# Revit family: QF_BOURGEAT_Self_Bain_marie_eau_3GN
name_source: partatom
category: Equipement spécialisé
revit_build: Autodesk Revit 2015 (Build: 20140606_1530(x64)
units: mm (PartAtom-declared; Revit-internal decimal feet)

## types (18) — shared parameters
Certification = NF alimentaire
Charge max = 200.00 kg
Cuve à air = Non
Cuve à eau = Oui
Diamètre de Raccordement Eau Adoucie = 21 mm
Diamètre de Raccordement Evacuation = 33 mm
Fabricant = BOURGEAT
Fréquence = 50 Hz
Indice de protection = 21
Longueur hors tout = 1209 mm  [stored 3.96654 ft]
Nature isolant = Laine de verre
Phase = 2
Profondeur hors tout = 820 mm  [stored 2.69029 ft]
Spécification du Fabricant = Bain-marie Oasis
Tension = 230 V
URL catalogue = http://www.bourgeat.fr
lg_etagere = 737 mm  [stored 2.41798 ft]
lg_porte = 379 mm
lg_presentoir = 1097 mm
lgconsole = 1165 mm  [stored 3.82218 ft]
lgmeuble = 1141 mm
zero-valued in all types: Hauteur de Raccordement Eau Adoucie du Sol Finis, Hauteur de Raccordement Evacuation Directe du Sol Finis

## per-type parameters (varying)
| type | Etageres | Hauteur hors tout | Intensité nominale | Modèle | Pieds | Poids net à vide | Presentoir | Puissance électrique  | Reserves | Roues |
| 3GN_baie_libre | Non | 900 mm | 9 A | 851033 | Oui | 150.00 kg | Non | 2100 W | Non | Non |
| 3GN_reserve | Non | 900 mm | 13 A | 851233 | Oui | 150.00 kg | Non | 3000 W | Oui | Non |
| 3GN_baie_libre+roues | Non | 900 mm | 9 A | 851033+854950 | Non | 150.00 kg | Non | 2100 W | Non | Oui |
| 3GN_baie_libre+etageres | Non | 900 mm | 9 A | 851033+854933 | Oui | 150.00 kg | Non | 2100 W | Non | Non |
| 3GN_baie_libre+presentoir_neutre | Non | 1330 mm | 9 A | 851033+851313 | Oui | 150.00 kg | Oui | 2100 W | Non | Non |
| 3GN_baie_libre+presentoir_chauffant | Non | 1330 mm | 11 A | 851033+851303 | Oui | 165.00 kg | Oui | 2580 W | Non | Non |
| 3GN_baie_libre+roues+etageres | Oui | 900 mm | 9 A | 851033+854950+854933 | Non | 150.00 kg | Non | 2100 W | Non | Oui |
| 3GN_baie_libre+roues+presentoir_neutre | Non | 1330 mm | 9 A | 851033+854950+851313 | Non | 165.00 kg | Oui | 2100 W | Non | Oui |
| 3GN_baie_libre+roues+presentoir_chauffant | Non | 1330 mm | 11 A | 851033+854950+851303 | Non | 165.00 kg | Oui | 2580 W | Non | Oui |
| 3GN_baie_libre+etageres+presentoir_neutre | Non | 1330 mm | 9 A | 851033+854933+851313 | Oui | 165.00 kg | Oui | 2100 W | Non | Non |
| 3GN_baie_libre+etageres+presentoir_chauffant | Non | 1330 mm | 11 A | 851033+854933+851303 | Oui | 165.00 kg | Oui | 2580 W | Non | Non |
| 3GN_baie_libre+roues+presentoir_neutre+etageres | Oui | 1330 mm | 9 A | 851033+854950+851313+854933 | Non | 165.00 kg | Oui | 2100 W | Non | Oui |
| 3GN_baie_libre+roues+presentoir_chauffant+etageres | Oui | 1330 mm | 11 A | 851033+854950+851313+854933 | Non | 165.00 kg | Oui | 2580 W | Non | Oui |
| 3GN_reserve+roues | Non | 900 mm | 13 A | 851233+854950 | Non | 150.00 kg | Non | 3000 W | Oui | Oui |
| 3GN_reserve+presentoir_neutre | Non | 1330 mm | 13 A | 851233+851313 | Non | 165.00 kg | Oui | 3000 W | Oui | Oui |
| 3GN_reserve+presentoir_chauffant | Non | 1330 mm | 15 A | 851233+851303 | Non | 165.00 kg | Oui | 3480 W | Oui | Oui |
| 3GN_reserve+roues+presentoir_neutre | Non | 1330 mm | 13 A | 851233+854950+851313 | Non | 165.00 kg | Oui | 3000 W | Oui | Oui |
| 3GN_reserve+roues+presentoir_chauffant | Non | 1330 mm | 15 A | 851233+854950+851303 | Non | 165.00 kg | Oui | 3480 W | Oui | Oui |

note: [stored X ft] marks values corroborated as IEEE doubles in the binary element streams (Revit-internal decimal feet)

## geometry (parser evidence)
native form markers: Blend x12
no freeform markers — native parametric forms only
